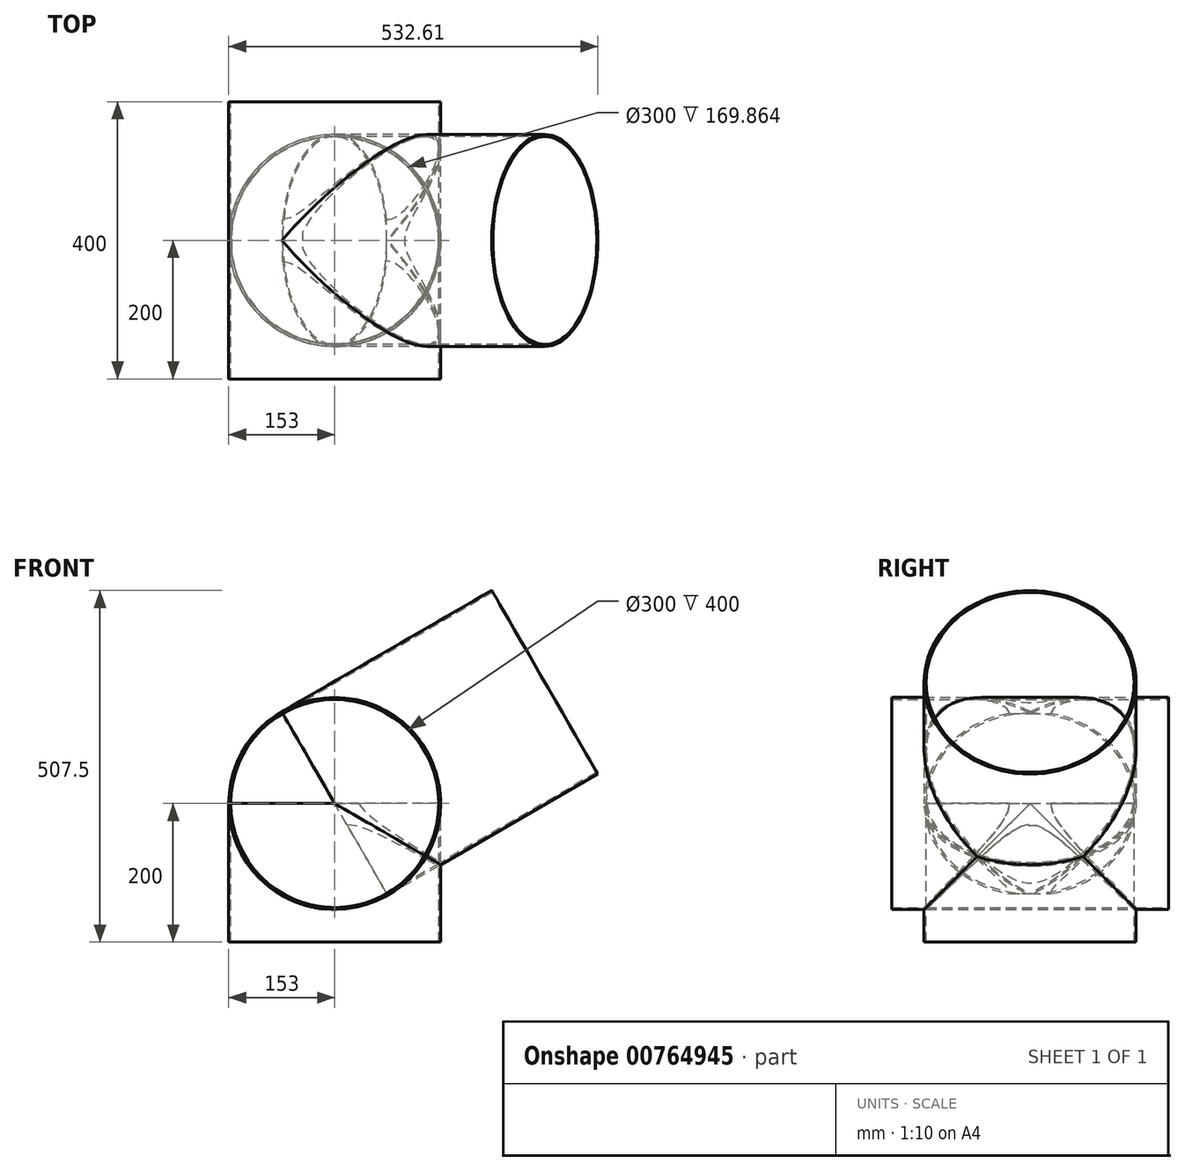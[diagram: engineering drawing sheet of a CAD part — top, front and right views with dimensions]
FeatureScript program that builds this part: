
annotation { "Feature Type Name" : "Feature", "Feature Type Description" : "" }
export const myFeature = defineFeature(function(context is Context, id is Id, definition is map)
    precondition{}
    {
        {
            var Q0;
            Q0=qCreatedBy(makeId("Front.planeOp"),FACE);
            var sketch = newSketch(context, id + "F0", { "sketchPlane" : qUnion([Q0])});
            skCircle(sketch, "E0", {"center": v(0, 0) * mm, "radius": 153 * mm});
            skCircle(sketch, "E1", {"center": v(0, 0) * mm, "radius": 150 * mm});
            skSolve(sketch);
        }
        {
            var Q0;
            Q0=makeQuery(id+"F0.imprint","IMPRINT",FACE,{"disambiguationData":[TD([[makeQuery(id+"F0.imprint","IMPRINT",EDGE,{"derivedFrom":sQuery(id+"F0.wireOp",EDGE,"E0")}),1.0]])]});
            extrude(context, id + "F1", {"entities" : qUnion([Q0]), "endBound" : BoundingType.SYMMETRIC, "depth" : 400 * mm, "offsetDistance" : 25 * mm});
        }
        {
            var Q0;
            Q0=qCreatedBy(makeId("Right.planeOp"),FACE);
            var Q1;
            Q1=makeQuery(id+"F1.opExtrude","SWEPT_FACE",FACE,{"disambiguationData":[OSD([sQuery(id+"F0.wireOp",EDGE,"E0")])]});
            cPlane(context, id + "F2", {"entities" : qUnion([Q0, Q1]), "cplaneType" : CPlaneType.LINE_ANGLE, "offset" : 25 * mm, "angle" : 150 * degree, "width" : 150 * mm, "height" : 150 * mm});
        }
        {
            var Q0;
            Q0=qCreatedBy(id+"F2.planeOp",FACE);
            var sketch = newSketch(context, id + "F3", { "sketchPlane" : qUnion([Q0])});
            skCircle(sketch, "E2", {"center": v(0, 0) * mm, "radius": 153 * mm});
            skCircle(sketch, "E3", {"center": v(0, 0) * mm, "radius": 150 * mm});
            skSolve(sketch);
        }
        {
            var Q0;
            Q0 = qSketchRegion(id + "F3", true);
            extrude(context, id + "F4", {"entities" : qUnion([Q0]), "operationType" : NewBodyOperationType.ADD, "depth" : 350 * mm, "offsetDistance" : 25 * mm});
        }
        {
            var Q0;
            Q0=qCreatedBy(makeId("Top.planeOp"),FACE);
            var sketch = newSketch(context, id + "F5", { "sketchPlane" : qUnion([Q0])});
            skCircle(sketch, "E4", {"center": v(0, 0) * mm, "radius": 153 * mm});
            skCircle(sketch, "E5", {"center": v(0, 0) * mm, "radius": 150 * mm});
            skSolve(sketch);
        }
        {
            var Q0;
            Q0 = qSketchRegion(id + "F5", true);
            var Q1;
            Q1=makeQuery(id+"Fm2BgVSejtAY0MA_1.1.FzRh5NedqIxXa94_1.opSweep","SWEPT_FACE",FACE,{"disambiguationData":[OSD([sQuery(id+"F5spO2P0RVahMae_1.wireOp",EDGE,"toN1d00U-fvSX-rbUA-DikX-AIDrSlOrtIeO"),sQuery(id+"FSML6lHRRHCVZ8a_1.wireOp",EDGE,"w4867379-E9La-xGKU-ABOE-A2VvsdeY1890")])]});
            extrude(context, id + "F6", {"entities" : qUnion([Q0]), "operationType" : NewBodyOperationType.ADD, "depth" : -200 * mm, "endBoundEntityFace" : qUnion([Q1]), "offsetDistance" : 25 * mm});
        }
        {
            var Q0;
            Q0=makeQuery(id+"F1.opExtrude","SWEPT_BODY",BODY,{"disambiguationData":[OSD([sQuery(id+"F0.wireOp",EDGE,"E0"),sQuery(id+"F0.wireOp",EDGE,"E1")])]});
            var Q1;
            Q1=qCreatedBy(makeId("Front.planeOp"),FACE);
            mirror(context, id + "F7", {"operationType" : NewBodyOperationType.ADD, "entities" : qUnion([Q0]), "mirrorPlane" : qUnion([Q1])});
        }
    });
